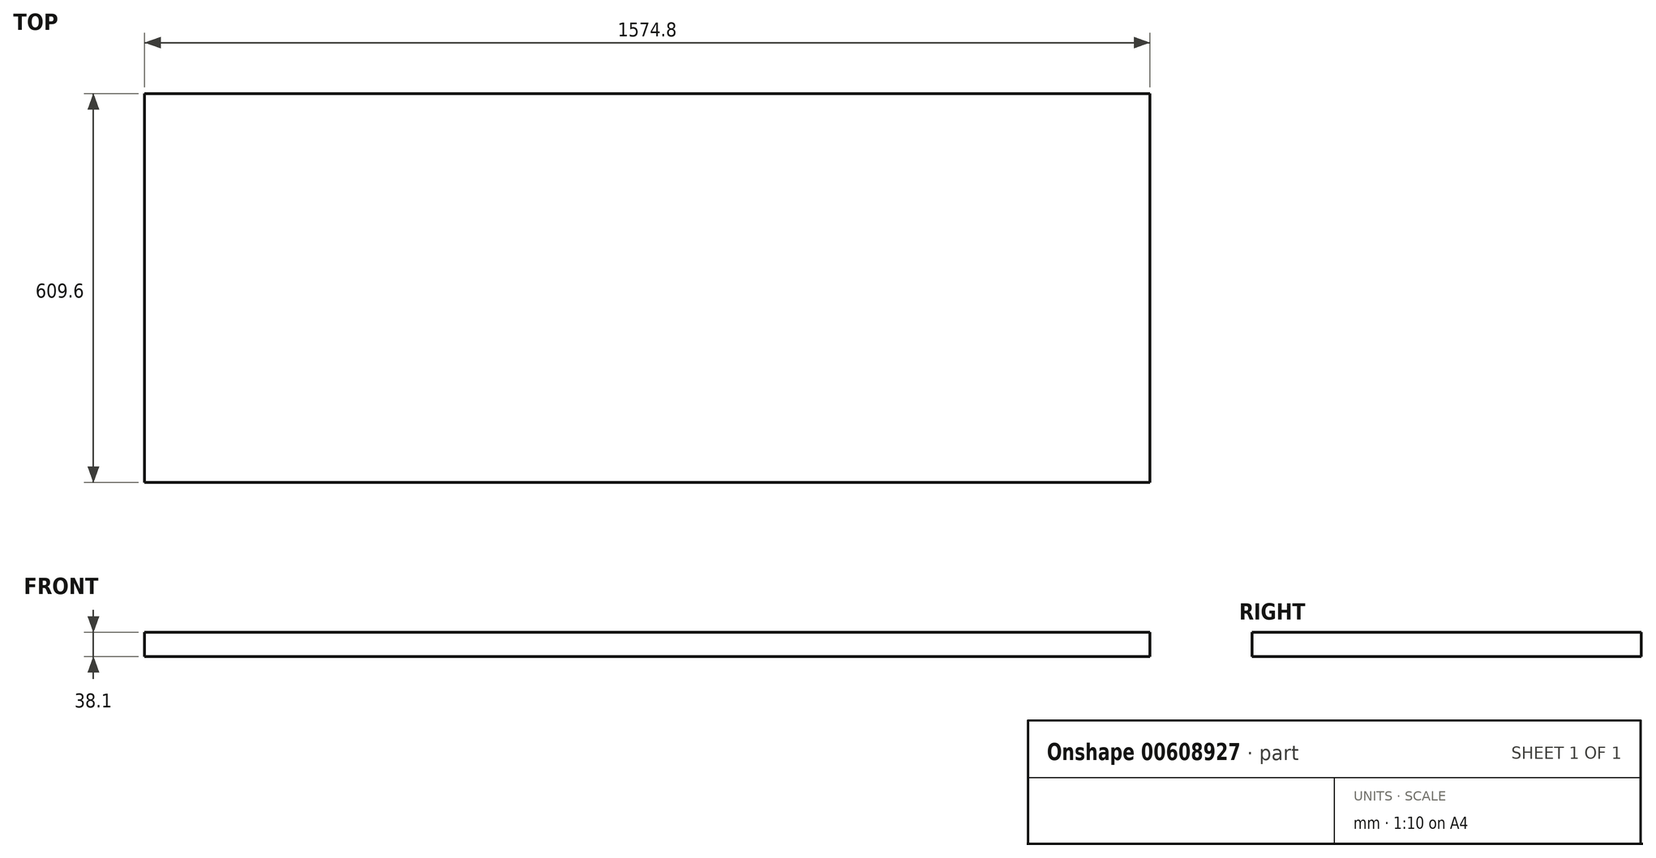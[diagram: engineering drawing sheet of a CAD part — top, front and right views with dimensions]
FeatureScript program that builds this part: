
annotation { "Feature Type Name" : "Feature", "Feature Type Description" : "" }
export const myFeature = defineFeature(function(context is Context, id is Id, definition is map)
    precondition{}
    {
        {
            var Q0;
            Q0=qCreatedBy(makeId("Top.planeOp"),FACE);
            var sketch = newSketch(context, id + "F0", { "sketchPlane" : qUnion([Q0])});
            skLineSegment(sketch, "E0.bottom", {"start": v(-784.04, -511.3) * mm, "end": v(790.76, -511.3) * mm});
            skLineSegment(sketch, "E0.top", {"start": v(-784.04, 98.3) * mm, "end": v(790.76, 98.3) * mm});
            skLineSegment(sketch, "E0.left", {"start": v(-784.04, -511.3) * mm, "end": v(-784.04, 98.3) * mm});
            skLineSegment(sketch, "E0.right", {"start": v(790.76, -511.3) * mm, "end": v(790.76, 98.3) * mm});
            skSolve(sketch);
        }
        {
            var Q0;
            Q0=makeQuery(id+"F0.imprint","IMPRINT",FACE,{"disambiguationData":[TD([[makeQuery(id+"F0.imprint","IMPRINT",EDGE,{"derivedFrom":sQuery(id+"F0.wireOp",EDGE,"E0.bottom")}),1.0]])]});
            extrude(context, id + "F1", {"entities" : qUnion([Q0]), "depth" : 38.1 * mm, "offsetDistance" : 25.4 * mm});
        }
    });
